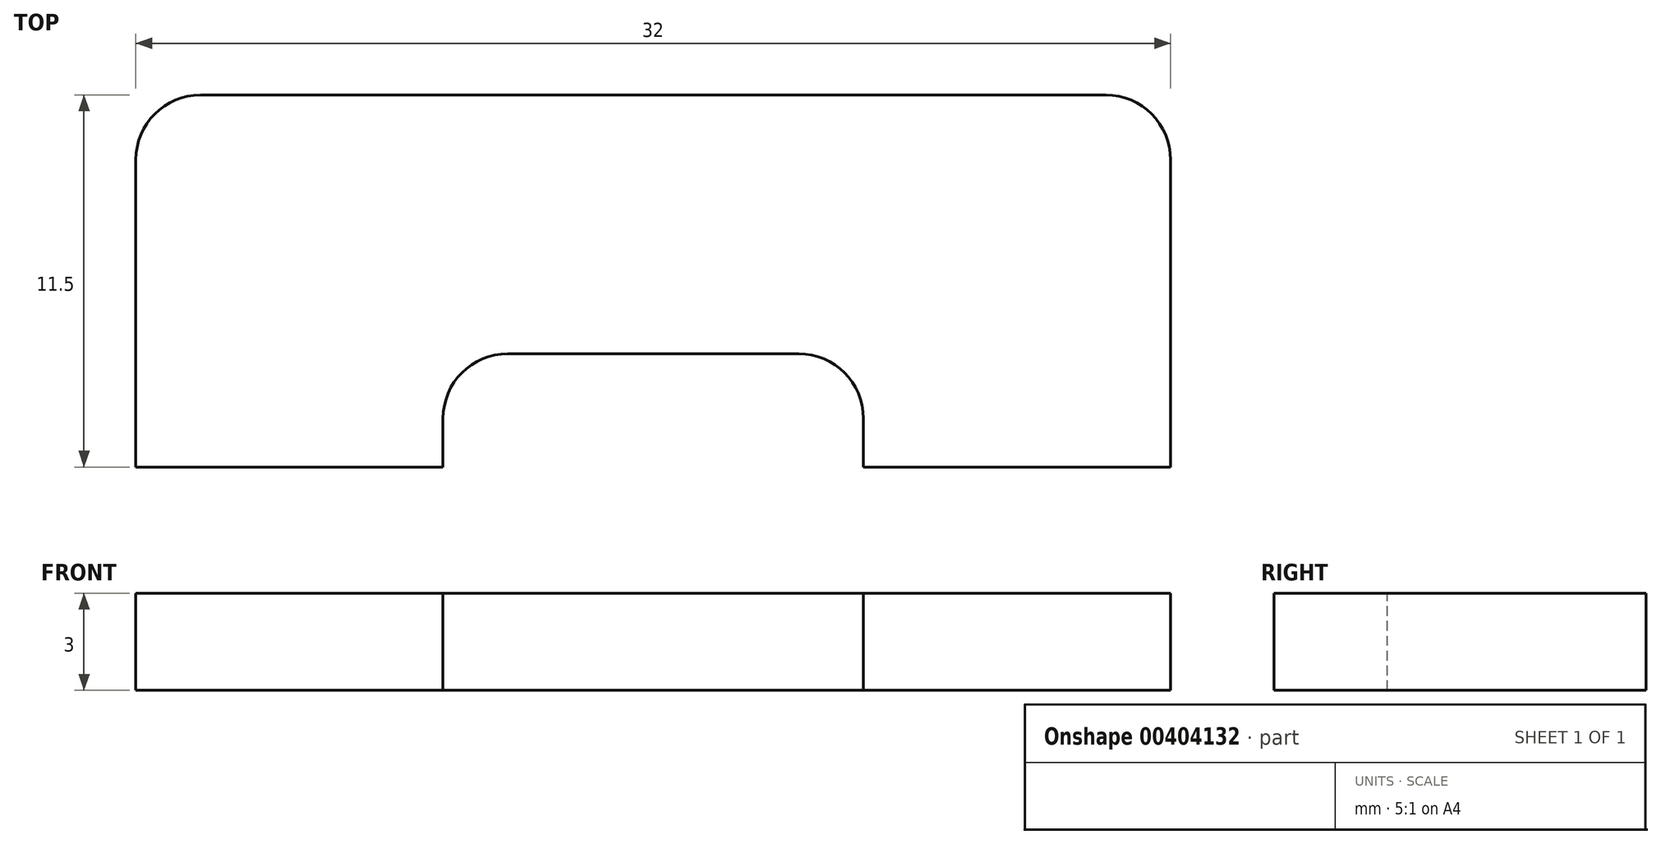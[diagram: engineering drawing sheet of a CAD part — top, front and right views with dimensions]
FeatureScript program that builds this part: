
annotation { "Feature Type Name" : "Feature", "Feature Type Description" : "" }
export const myFeature = defineFeature(function(context is Context, id is Id, definition is map)
    precondition{}
    {
        {
            var Q0;
            Q0=qCreatedBy(makeId("Top.planeOp"),FACE);
            var sketch = newSketch(context, id + "F0", { "sketchPlane" : qUnion([Q0])});
            skLineSegment(sketch, "E0.bottom", {"start": v(-16, 11.5) * mm, "end": v(16, 11.5) * mm});
            skLineSegment(sketch, "E0.top", {"start": v(-16, 0) * mm, "end": v(16, 0) * mm});
            skLineSegment(sketch, "E0.left", {"start": v(-16, 11.5) * mm, "end": v(-16, 0) * mm});
            skLineSegment(sketch, "E0.right", {"start": v(16, 11.5) * mm, "end": v(16, 0) * mm});
            skSolve(sketch);
        }
        {
            var Q0;
            Q0=qSketchRegion(id+"F0",true);
            extrude(context, id + "F1", {"entities" : qUnion([Q0]), "depth" : 3 * mm});
        }
        {
            var Q0;
            Q0=makeQuery(id+"F1.opExtrude","SWEPT_EDGE",EDGE,{"disambiguationData":[OSD([sQuery(id+"F0.wireOp",EDGE,"E0.bottom"),sQuery(id+"F0.wireOp",EDGE,"E0.left")])]});
            var Q1;
            Q1=makeQuery(id+"F1.opExtrude","SWEPT_EDGE",EDGE,{"disambiguationData":[OSD([sQuery(id+"F0.wireOp",EDGE,"E0.bottom"),sQuery(id+"F0.wireOp",EDGE,"E0.right")])]});
            fillet(context, id + "F2", {"entities" : qUnion([Q0, Q1]), "radius" : 2 * mm, "tangentPropagation" : true, "allowEdgeOverflow" : false});
        }
        {
            var Q0;
            Q0=makeQuery(id+"F1.opExtrude","CAP_FACE",FACE,{"disambiguationData":[OSD([sQuery(id+"F0.wireOp",EDGE,"E0.bottom"),sQuery(id+"F0.wireOp",EDGE,"E0.top"),sQuery(id+"F0.wireOp",EDGE,"E0.left"),sQuery(id+"F0.wireOp",EDGE,"E0.right")])],"isStart":false});
            var sketch = newSketch(context, id + "F3", { "sketchPlane" : qUnion([Q0])});
            skLineSegment(sketch, "E1.bottom", {"start": v(-6.5, 3.5) * mm, "end": v(6.5, 3.5) * mm});
            skLineSegment(sketch, "E1.top", {"start": v(-6.5, 0) * mm, "end": v(6.5, 0) * mm});
            skLineSegment(sketch, "E1.left", {"start": v(-6.5, 3.5) * mm, "end": v(-6.5, 0) * mm});
            skLineSegment(sketch, "E1.right", {"start": v(6.5, 3.5) * mm, "end": v(6.5, 0) * mm});
            skSolve(sketch);
        }
        {
            var Q0;
            Q0=qSketchRegion(id+"F3",true);
            extrude(context, id + "F4", {"entities" : qUnion([Q0]), "operationType" : NewBodyOperationType.REMOVE, "endBound" : BoundingType.THROUGH_ALL, "oppositeDirection" : true, "depth" : 25 * mm});
        }
        {
            var Q0;
            Q0=makeQuery(id+"F4.boolean.opBoolean","COPY",EDGE,{"derivedFrom":makeQuery(id+"F4.opExtrude","SWEPT_EDGE",EDGE,{"disambiguationData":[OSD([sQuery(id+"F3.wireOp",EDGE,"E1.bottom"),sQuery(id+"F3.wireOp",EDGE,"E1.left")])]})});
            var Q1;
            Q1=makeQuery(id+"F4.boolean.opBoolean","COPY",EDGE,{"derivedFrom":makeQuery(id+"F4.opExtrude","SWEPT_EDGE",EDGE,{"disambiguationData":[OSD([sQuery(id+"F3.wireOp",EDGE,"E1.bottom"),sQuery(id+"F3.wireOp",EDGE,"E1.right")])]})});
            fillet(context, id + "F5", {"entities" : qUnion([Q0, Q1]), "radius" : 2 * mm, "tangentPropagation" : true, "allowEdgeOverflow" : false});
        }
    });
